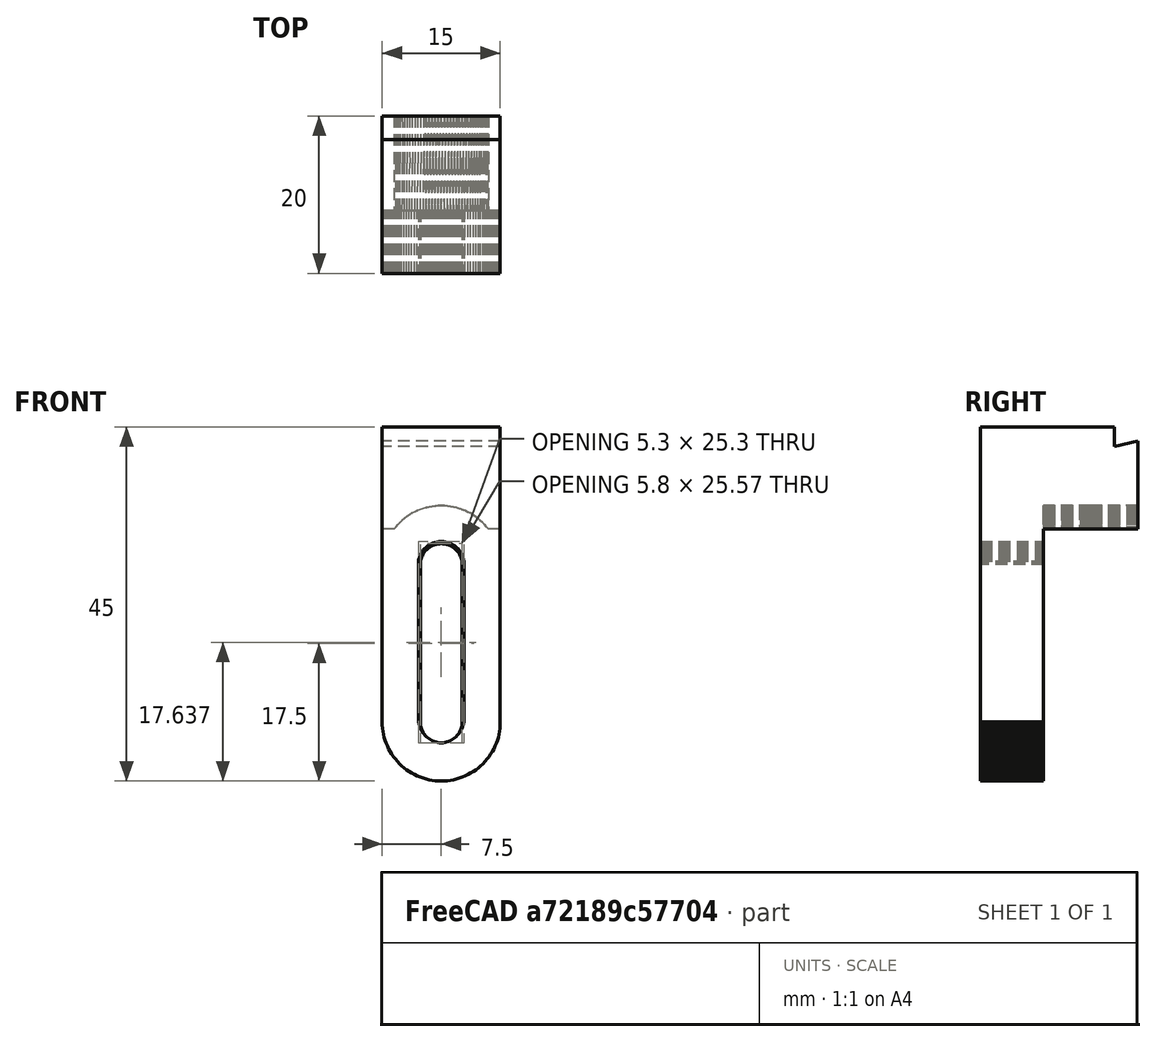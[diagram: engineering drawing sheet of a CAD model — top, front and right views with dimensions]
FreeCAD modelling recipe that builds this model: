
FCSTD DOCUMENT  (FreeCAD 1.2R44936 (Git))
Label: PCB_Support_Long_modified
License: All rights reserved
LicenseURL: https://en.wikipedia.org/wiki/All_rights_reserved
objects: Part::Feature×3, Part::Refine×2, Mesh::Feature×1, App::Point×1, PartDesign::ShapeBinder×1, Sketcher::SketchObject×1, PartDesign::FeatureBase×1, PartDesign::Pocket×1, PartDesign::Body×1
note: 14 computed .brp shape members not serialized (recipe doc carries the construction recipe); baked Part::Feature solids carry a one-line shape summary decoded from their .brp

FEATURE [Mesh::Feature] PCB_Support_Long
FEATURE [Part::Feature] PCB_Support_Long001
  shape: bbox 15 x 20 x 45 mm, 922 faces, 0 solids (baked)
FEATURE [Part::Feature] PCB_Support_Long001_solid  label="PCB_Support_Long001 (Solid)"
  shape: bbox 15 x 20 x 45 mm, 922 faces (baked)
FEATURE [Part::Refine] PCB_Support_Long001_solid001  label="PCB_Support_Long001 (Solid)001"
  Source = -> PCB_Support_Long001_solid
FEATURE [App::Point] Origin001
  Role = Origin
FEATURE [PartDesign::ShapeBinder] CopyPCB_Support_Long001_solid001
  TraceSupport = false
FEATURE [Sketcher::SketchObject] Sketch
  ArcFitTolerance = 1e-06
  AttachmentSupport = -> [CopyPCB_Support_Long001_solid001]
  ExternalTypes = [0]
  FullyConstrained = true
  MakeInternals = false
  MapMode = 5
  Placement = pos=(0,8,0) rot=(0,0.707107,0.707107;3.14159rad)
  sketch-geometry (4):
    g0: ArcOfCircle CenterX=0 CenterY=0 CenterZ=0 NormalX=0 NormalY=0 NormalZ=1 AngleXU=0 Radius=2.925 StartAngle=0.130837 EndAngle=3.01076
    g1: ArcOfCircle CenterX=-1e-16 CenterY=-19.6184 CenterZ=0 NormalX=0 NormalY=0 NormalZ=1 AngleXU=0 Radius=2.9 StartAngle=3.14159 EndAngle=6.28319
    g2: LineSegment StartX=-2.9 StartY=-19.6184 StartZ=0 EndX=-2.9 EndY=0.381608 EndZ=0
    g3: LineSegment StartX=2.9 StartY=-19.6184 StartZ=0 EndX=2.9 EndY=0.381608 EndZ=0
  constraints (11):
    c: Coincident(g0,g-1)
    c: Vertical(g2)
    c: Vertical(g3)
    c: Diameter(g0) = 5.85
    c: Coincident(g2,g0)
    c: Coincident(g3,g0)
    c: Diameter(g1) = 5.8
    c: Tangent(g2,g1) = 1.5708
    c: Tangent(g3,g1) = -1.5708
    c: DistanceY(g3,g3) = 20
    c: Equal(g3,g2)
FEATURE [Part::Feature] PCB_Support_Long001_solid002  label="PCB_Support_Long001 (Solid)002"
  shape: bbox 15 x 20 x 45 mm, 922 faces (baked)
FEATURE [Part::Refine] PCB_Support_Long001_solid003  label="PCB_Support_Long001 (Solid)003"
  Source = -> PCB_Support_Long001_solid002
FEATURE [PartDesign::FeatureBase] BaseFeature
  BaseFeature = -> PCB_Support_Long001_solid003
  Suppressed = false
FEATURE [PartDesign::Pocket] Pocket
  BaseFeature = -> BaseFeature
  Direction = (0,-1,2e-16)
  Length = 5
  Length2 = 5
  Profile = -> Sketch
  ReferenceAxis = -> Sketch [N_Axis]
  Refine = true
  SideType = 0
  Suppressed = false
  Type = 1
  Type2 = 0
FEATURE [PartDesign::Body] Body
  AllowCompound = true
  BaseFeature = -> PCB_Support_Long001_solid003
  Group = -> [BaseFeature,CopyPCB_Support_Long001_solid001,Sketch,Pocket]
  Origin = -> Origin
  Tip = -> Pocket
